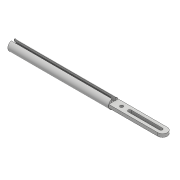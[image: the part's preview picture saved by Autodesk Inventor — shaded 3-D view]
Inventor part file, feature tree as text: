
AUTODESK INVENTOR PART (.ipt)
format: ipt  version: 2017 (Build 210142000, 142)  size: 128,000 bytes
history: native  units: mm
features: extrude x4, sketch x4, plane x2, hole x1
ambient origin geometry x8: Origin, YZ Plane, XZ Plane, XY Plane, X Axis, Y Axis, Z Axis, Center Point
bodies: Solid1 (feature_tree)
feature tree (11):
  extrude  "Extrusion1"  Depth=10.0mm
  plane  "Work Plane1"
  extrude  "Extrusion2"  Depth=585.0mm
  extrude  "Extrusion3"  [1 undecoded]
  hole  "Hole1"  [1 undecoded]
  plane  "Work Plane2"
  extrude  "Extrusion4"  Depth=10.0mm
  sketch  "Sketch1"  dims[d0=100.0mm d1=10.0mm]
  sketch  "Sketch2"  dims[d3=20.0mm d6=585.0mm]
  sketch  "Sketch3"  dims[d7=10.0mm d8=0.0mm d9=-151.0mm]
  sketch  "Sketch4"  dims[d10=320.0mm d11=0.0mm d12=169.0mm d13=0.0mm d14=10.0mm d15=10.0mm d16=20.0mm d17=6.0mm d18=4.0mm d19=2.0mm d20=90.0deg d21=305.0mm d22=20.594885mm d23=19.5mm d24=10.0mm d25=10.0mm d26=25.5mm d27=0.0mm]
note: 2 required parameter values undecoded (feature->parameter linkage not recoverable at this tier; creation-order binding heuristic only, values carry confidence <= 0.55)
